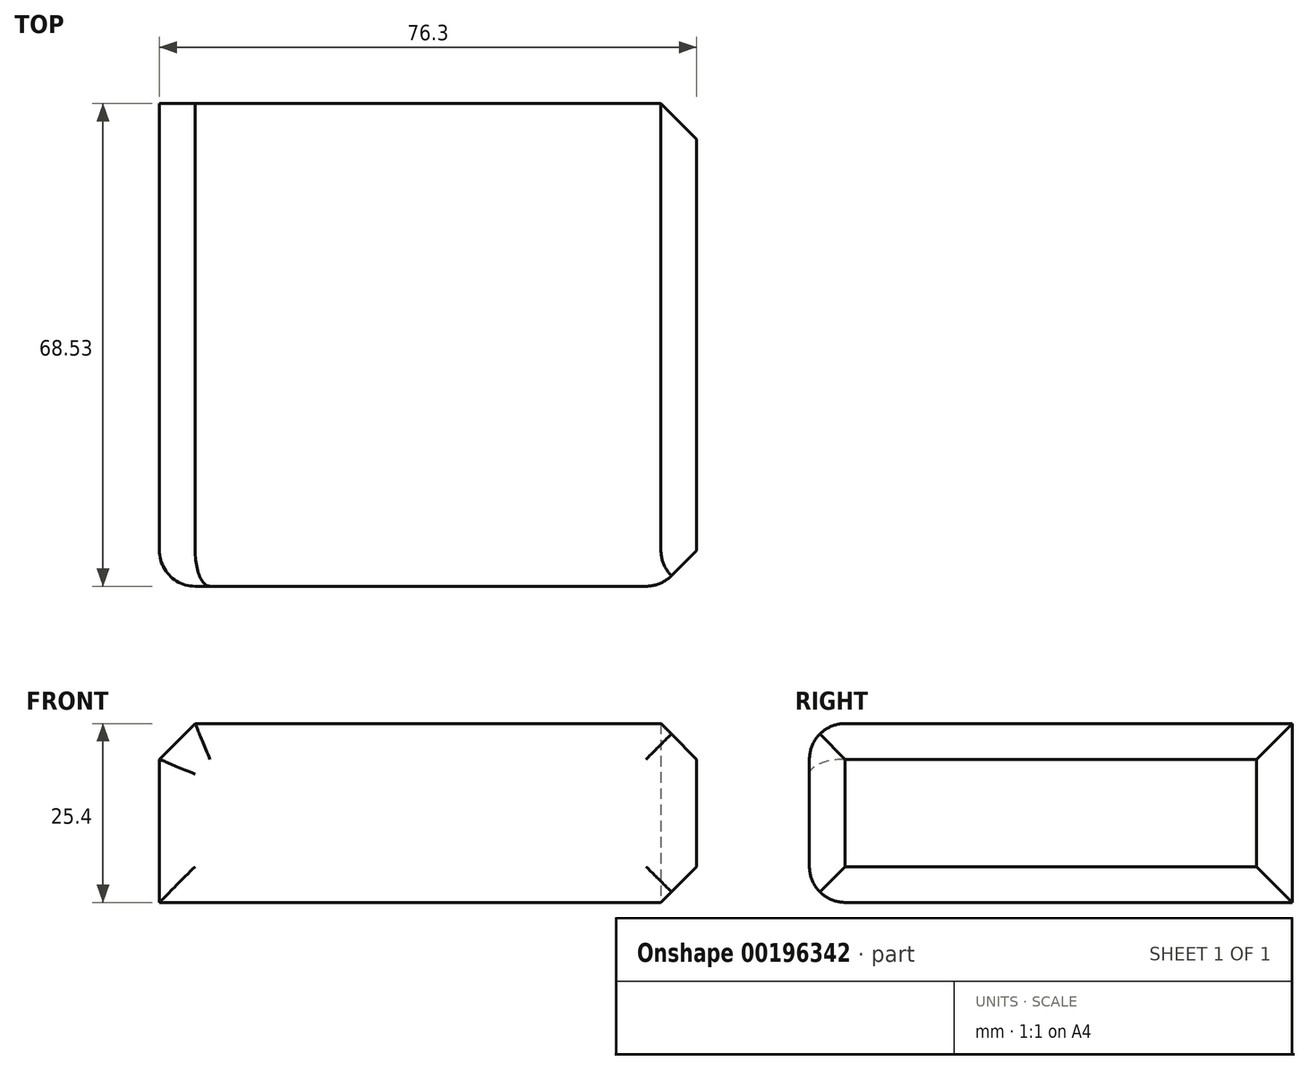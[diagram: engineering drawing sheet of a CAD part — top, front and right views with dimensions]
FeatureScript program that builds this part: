
annotation { "Feature Type Name" : "Feature", "Feature Type Description" : "" }
export const myFeature = defineFeature(function(context is Context, id is Id, definition is map)
    precondition{}
    {
        {
            var Q0;
            Q0=qCreatedBy(makeId("Top.planeOp"),FACE);
            var sketch = newSketch(context, id + "F0", { "sketchPlane" : qUnion([Q0])});
            skLineSegment(sketch, "E0.bottom", {"start": v(-40.13, 36.58) * mm, "end": v(36.17, 36.58) * mm});
            skLineSegment(sketch, "E0.top", {"start": v(-40.13, -31.95) * mm, "end": v(36.17, -31.95) * mm});
            skLineSegment(sketch, "E0.left", {"start": v(-40.13, 36.58) * mm, "end": v(-40.13, -31.95) * mm});
            skLineSegment(sketch, "E0.right", {"start": v(36.17, 36.58) * mm, "end": v(36.17, -31.95) * mm});
            skSolve(sketch);
        }
        {
            var Q0;
            Q0=makeQuery(id+"F0.imprint","IMPRINT",FACE,{"disambiguationData":[TD([[makeQuery(id+"F0.imprint","IMPRINT",EDGE,{"derivedFrom":sQuery(id+"F0.wireOp",EDGE,"E0.bottom")}),-1.0]])]});
            extrude(context, id + "F1", {"entities" : qUnion([Q0]), "depth" : 25.4 * mm});
        }
        {
            var Q0;
            Q0=makeQuery(id+"F1.opExtrude","SWEPT_FACE",FACE,{"disambiguationData":[OSD([sQuery(id+"F0.wireOp",EDGE,"E0.right")])]});
            var Q1;
            Q1=makeQuery(id+"F1.opExtrude","CAP_EDGE",EDGE,{"disambiguationData":[OSD([sQuery(id+"F0.wireOp",EDGE,"E0.left")])],"isStart":false});
            chamfer(context, id + "F2", {"entities" : qUnion([Q0, Q1]), "width" : 5.08 * mm, "tangentPropagation" : true});
        }
        {
            var Q0;
            Q0=makeQuery(id+"F1.opExtrude","SWEPT_FACE",FACE,{"disambiguationData":[OSD([sQuery(id+"F0.wireOp",EDGE,"E0.top")])]});
            fillet(context, id + "F3", {"entities" : qUnion([Q0]), "radius" : 5.08 * mm, "tangentPropagation" : true, "allowEdgeOverflow" : false});
        }
    });
